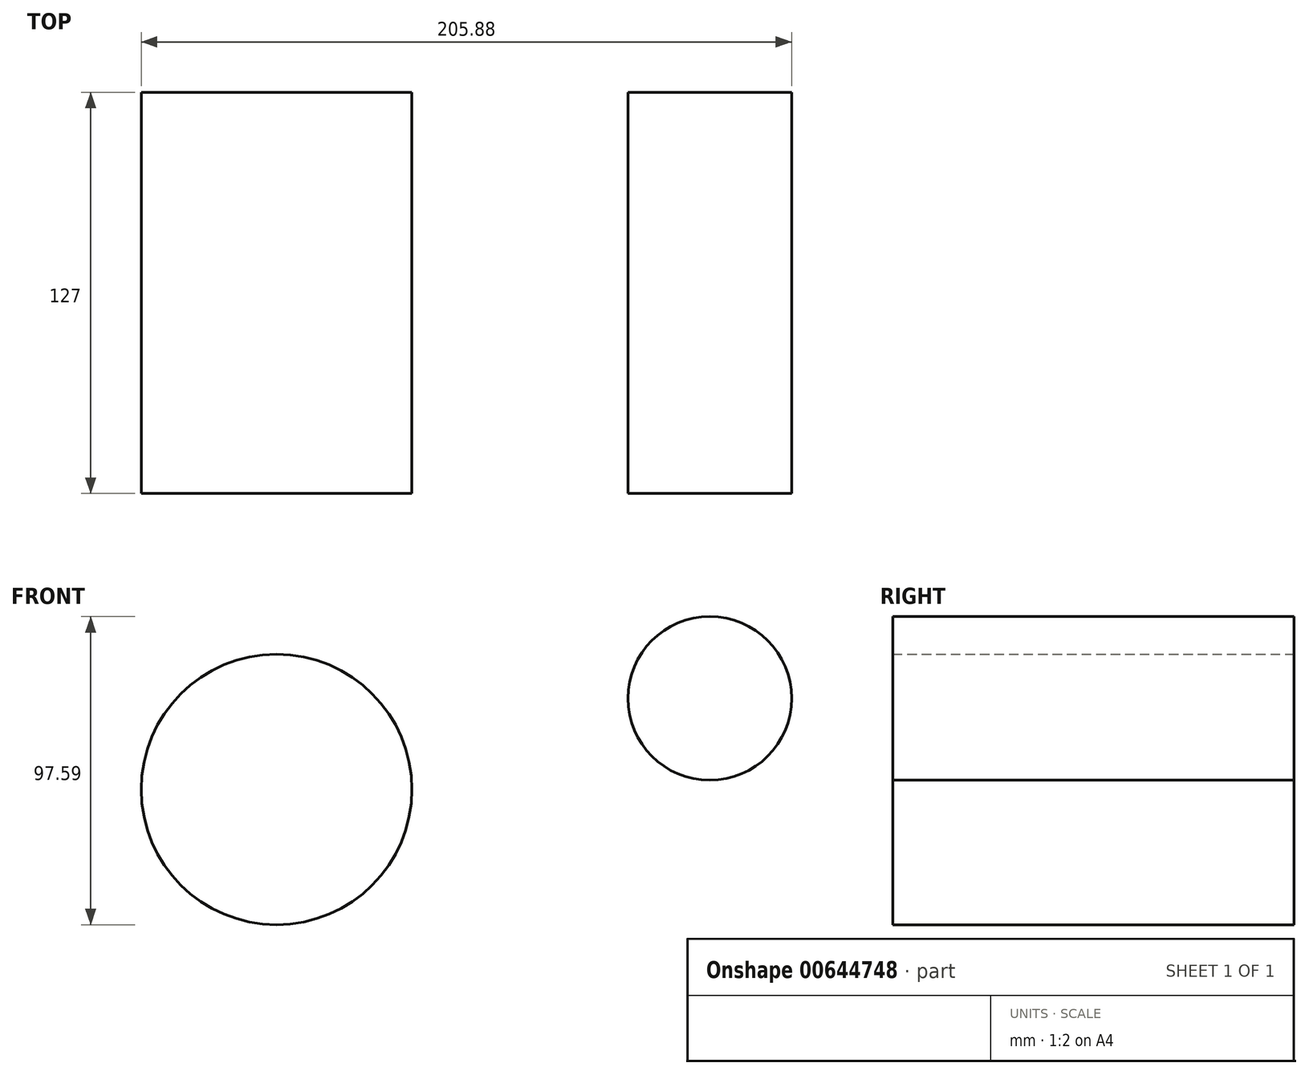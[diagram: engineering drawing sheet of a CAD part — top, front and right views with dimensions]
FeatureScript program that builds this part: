
annotation { "Feature Type Name" : "Feature", "Feature Type Description" : "" }
export const myFeature = defineFeature(function(context is Context, id is Id, definition is map)
    precondition{}
    {
        {
            var Q0;
            Q0=qCreatedBy(makeId("Front.planeOp"),FACE);
            var sketch = newSketch(context, id + "F0", { "sketchPlane" : qUnion([Q0])});
            skCircle(sketch, "E0", {"center": v(14.31, -16.39) * mm, "radius": 42.84 * mm});
            skSolve(sketch);
        }
        {
            var Q0;
            Q0=qCreatedBy(makeId("Front.planeOp"),FACE);
            var sketch = newSketch(context, id + "F1", { "sketchPlane" : qUnion([Q0])});
            skCircle(sketch, "E1", {"center": v(151.44, 12.45) * mm, "radius": 25.91 * mm});
            skSolve(sketch);
        }
        {
            var Q0;
            Q0=makeQuery(id+"F0.imprint","IMPRINT",FACE,{"disambiguationData":[TD([[makeQuery(id+"F0.imprint","IMPRINT",EDGE,{"derivedFrom":sQuery(id+"F0.wireOp",EDGE,"E0")}),1.0]])]});
            var sketch = newSketch(context, id + "F2", { "sketchPlane" : qUnion([Q0])});
            skLineSegment(sketch, "E2", {"start": v(25.3, -58.3) * mm, "end": v(159.33, -12.45) * mm});
            skLineSegment(sketch, "E3", {"start": v(0, 25.52) * mm, "end": v(146.46, 38.17) * mm});
            skSolve(sketch);
        }
        {
            var Q0;
            Q0=makeQuery(id+"F1.imprint","IMPRINT",FACE,{"disambiguationData":[TD([[makeQuery(id+"F1.imprint","IMPRINT",EDGE,{"derivedFrom":sQuery(id+"F1.wireOp",EDGE,"E1")}),1.0]])]});
            var Q1;
            Q1 = qSketchRegion(id + "F0", true);
            var Q2;
            Q2 = qSketchRegion(id + "F2", true);
            var Q3;
            Q3=makeQuery(id+"F2.imprint","IMPRINT",FACE,{"disambiguationData":[TD([[makeQuery(id+"F2.imprint","IMPRINT",EDGE,{"derivedFrom":makeQuery(id+"F0.imprint","IMPRINT",EDGE,{"derivedFrom":sQuery(id+"F0.wireOp",EDGE,"E0")})}),1.0]])]});
            extrude(context, id + "F3", {"entities" : qUnion([Q0, Q1, Q2, Q3]), "depth" : 127 * mm, "offsetDistance" : 25.4 * mm});
        }
    });
